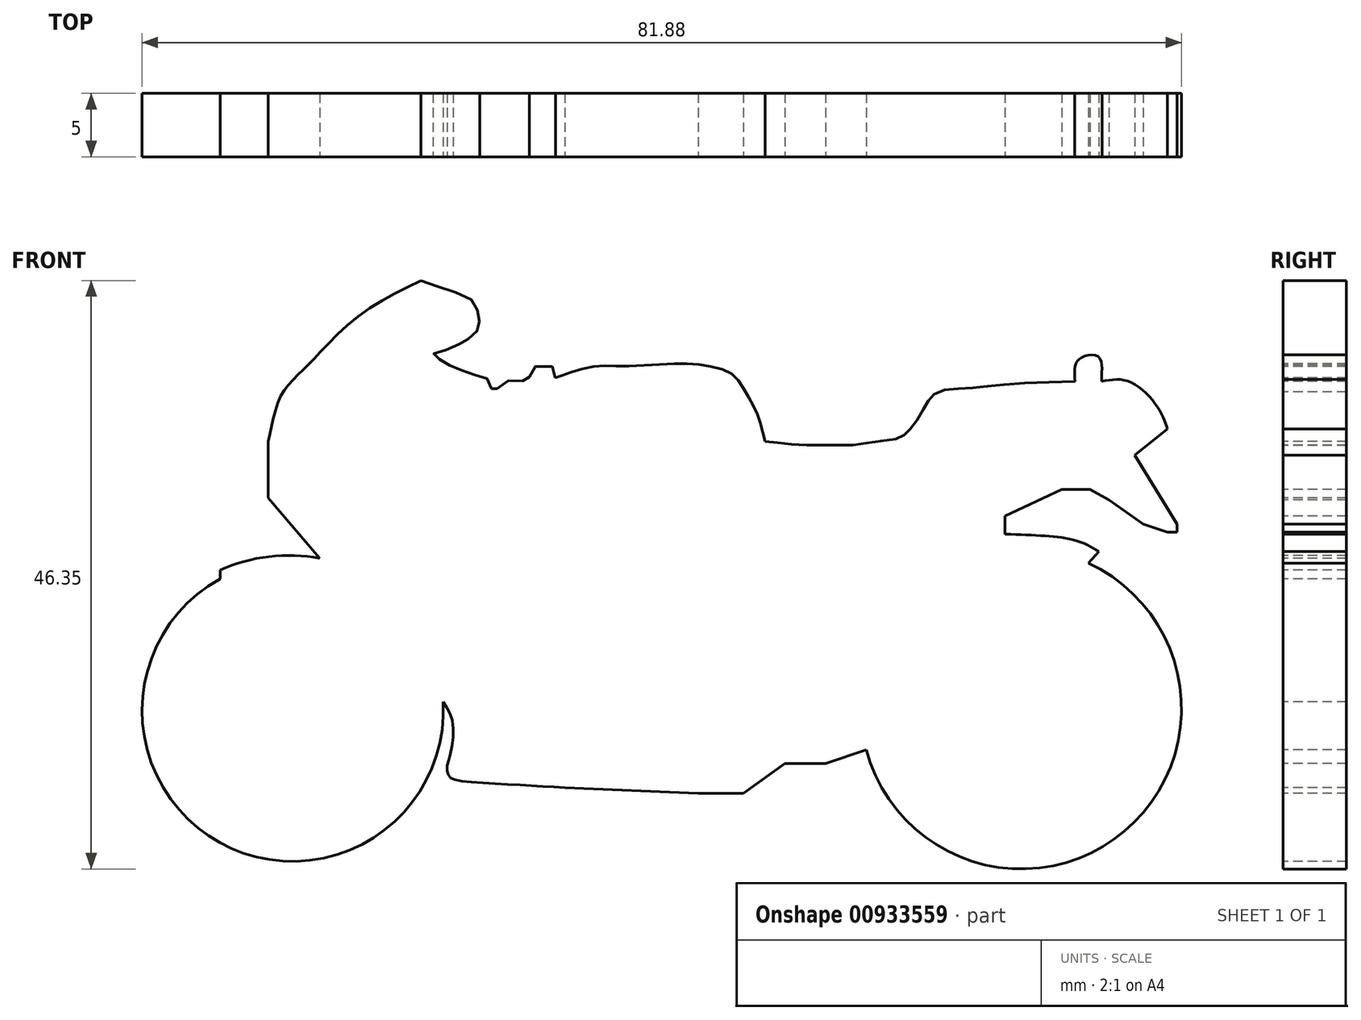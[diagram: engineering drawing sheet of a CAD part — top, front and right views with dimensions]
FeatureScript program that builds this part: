
annotation { "Feature Type Name" : "Feature", "Feature Type Description" : "" }
export const myFeature = defineFeature(function(context is Context, id is Id, definition is map)
    precondition{}
    {
        {
            var Q0;
            Q0=qCreatedBy(makeId("Front.planeOp"),FACE);
            var sketch = newSketch(context, id + "F0", { "sketchPlane" : qUnion([Q0])});
            skArc(sketch, "E0", {"start": v(-70.16, 1.42) * mm, "mid": v(-70.21, -40.14) * mm, "end": v(-35.04, -18) * mm});
            skArc(sketch, "E1", {"start": v(-54.46, 4.66) * mm, "mid": v(-62.45, 4.92) * mm, "end": v(-70.16, 2.8) * mm});
            skLineSegment(sketch, "E2", {"start": v(-70.16, 2.8) * mm, "end": v(-70.16, 1.42) * mm});
            skLineSegment(sketch, "E3", {"start": v(-54.46, 4.66) * mm, "end": v(-62.6, 14.14) * mm});
            skLineSegment(sketch, "E4", {"start": v(-62.6, 23.05) * mm, "end": v(-62.6, 14.14) * mm});
            skFitSpline(sketch, "E5", {"points": [v(-62.6, 23.05) * mm, v(-61.9, 26.19) * mm, v(-60.75, 29.94) * mm, v(-59.4, 31.96) * mm, v(-57.38, 34.08) * mm, v(-54.97, 36.48) * mm, v(-48.72, 42.54) * mm, v(-38.52, 48.41) * mm], "startDerivative": vector(5.38, 25.5) * mm, "endDerivative": vector(48.04, 23.54) * mm});
            skFitSpline(sketch, "E6", {"points": [v(-38.52, 48.41) * mm, v(-34.38, 46.97) * mm, v(-30.34, 45.24) * mm, v(-29.57, 43.4) * mm, v(-29.28, 41.68) * mm, v(-29.76, 40.33) * mm, v(-31.3, 39.08) * mm, v(-32.65, 38.3) * mm, v(-35.34, 37.25) * mm, v(-36.6, 36.77) * mm, v(-35.44, 35.9) * mm, v(-33.8, 34.94) * mm, v(-31.59, 34.08) * mm, v(-29, 33.2) * mm, v(-27.55, 32.44) * mm, v(-27.26, 30.9) * mm, v(-25.82, 32.06) * mm, v(-23.6, 32.73) * mm, v(-21.49, 32.73) * mm, v(-21.3, 34.36) * mm, v(-17.83, 34.85) * mm, v(-17.35, 33.11) * mm], "startDerivative": vector(57.73, -21.29) * mm, "endDerivative": vector(-4, -47.72) * mm});
            skFitSpline(sketch, "E7", {"points": [v(-17.35, 33.11) * mm, v(-15.32, 33.8) * mm, v(-11.03, 34.9) * mm, v(-6.58, 34.9) * mm, v(0.95, 35.3) * mm, v(6.13, 35.06) * mm, v(10.25, 33.8) * mm, v(12.11, 31.66) * mm, v(13.9, 28.67) * mm, v(14.95, 26) * mm, v(15.67, 23.05) * mm], "startDerivative": vector(24.4, 8.5) * mm, "endDerivative": vector(7.65, -34.2) * mm});
            skFitSpline(sketch, "E8", {"points": [v(15.67, 23.05) * mm, v(18.48, 22.76) * mm, v(22.2, 22.47) * mm, v(26.77, 22.47) * mm, v(30.05, 22.55) * mm, v(33.2, 23.05) * mm, v(36.73, 23.56) * mm, v(37.78, 24.21) * mm, v(38.7, 25.18) * mm, v(40.04, 27.08) * mm, v(41.14, 28.99) * mm, v(41.87, 30.04) * mm, v(43.17, 30.96) * mm, v(46.23, 31.37) * mm, v(49.7, 31.64) * mm, v(54.53, 32.11) * mm, v(64.54, 32.5) * mm], "startDerivative": vector(45.35, -4.7) * mm, "endDerivative": vector(95.81, 2.47) * mm});
            skFitSpline(sketch, "E9", {"points": [v(64.54, 32.5) * mm, v(64.54, 34.85) * mm, v(65.6, 36.3) * mm, v(68.26, 36.35) * mm, v(68.75, 33.8) * mm, v(68.75, 32.5) * mm], "startDerivative": vector(-1.02, 11.74) * mm, "endDerivative": vector(0.17, -6.99) * mm});
            skFitSpline(sketch, "E10", {"points": [v(68.75, 32.5) * mm, v(73.05, 32.5) * mm, v(77.57, 28.43) * mm, v(79.11, 25.02) * mm], "startDerivative": vector(13.35, 2.6) * mm, "endDerivative": vector(3.66, -10.87) * mm});
            skLineSegment(sketch, "E11", {"start": v(79.11, 25.02) * mm, "end": v(73.96, 20.89) * mm});
            skLineSegment(sketch, "E12", {"start": v(73.96, 20.89) * mm, "end": v(80.6, 10.07) * mm});
            skLineSegment(sketch, "E13", {"start": v(80.6, 10.07) * mm, "end": v(80.6, 8.77) * mm});
            skLineSegment(sketch, "E14", {"start": v(80.6, 8.77) * mm, "end": v(79.11, 8.77) * mm});
            skLineSegment(sketch, "E15", {"start": v(79.11, 8.77) * mm, "end": v(75.26, 10.07) * mm});
            skLineSegment(sketch, "E16", {"start": v(75.26, 10.07) * mm, "end": v(69.87, 13.88) * mm});
            skLineSegment(sketch, "E17", {"start": v(69.87, 13.88) * mm, "end": v(66.89, 15.51) * mm});
            skLineSegment(sketch, "E18", {"start": v(66.89, 15.51) * mm, "end": v(62.41, 15.51) * mm});
            skLineSegment(sketch, "E19", {"start": v(62.41, 15.51) * mm, "end": v(53.51, 11.3) * mm});
            skLineSegment(sketch, "E20", {"start": v(53.51, 11.3) * mm, "end": v(53.51, 8.48) * mm});
            skFitSpline(sketch, "E21", {"points": [v(53.51, 8.48) * mm, v(59.2, 8.22) * mm, v(62.97, 7.85) * mm, v(66.2, 6.88) * mm, v(68.25, 5.73) * mm], "startDerivative": vector(19.3, -0.82) * mm, "endDerivative": vector(9.61, -5.99) * mm});
            skLineSegment(sketch, "E22", {"start": v(68.25, 5.73) * mm, "end": v(66.61, 3.89) * mm});
            skArc(sketch, "E23", {"start": v(31.64, -25.54) * mm, "mid": v(72.3, -38.37) * mm, "end": v(66.61, 3.89) * mm});
            skLineSegment(sketch, "E24", {"start": v(31.64, -25.54) * mm, "end": v(25.22, -27.66) * mm});
            skLineSegment(sketch, "E25", {"start": v(25.22, -27.66) * mm, "end": v(18.81, -27.66) * mm});
            skLineSegment(sketch, "E26", {"start": v(18.81, -27.66) * mm, "end": v(12.3, -32.35) * mm});
            skLineSegment(sketch, "E27", {"start": v(12.3, -32.35) * mm, "end": v(5.2, -32.35) * mm});
            skLineSegment(sketch, "E28", {"start": v(5.2, -32.35) * mm, "end": v(-15.86, -31.48) * mm});
            skFitSpline(sketch, "E29", {"points": [v(-15.86, -31.48) * mm, v(-24.83, -30.97) * mm, v(-32.93, -30.3) * mm, v(-34.09, -29.67) * mm, v(-34.4, -28.33) * mm, v(-33.8, -25.82) * mm, v(-33.6, -20.92) * mm, v(-35.04, -18) * mm], "startDerivative": vector(-39.5, 2.3) * mm, "endDerivative": vector(-13.64, 19.69) * mm});
            skSolve(sketch);
        }
        {
            var Q0;
            Q0=qCreatedBy(makeId("Front.planeOp"),FACE);
            var sketch = newSketch(context, id + "F1", { "sketchPlane" : qUnion([Q0])});
            skFitSpline(sketch, "E30", {"points": [v(-35.04, -17.89) * mm, v(-36.13, -15.41) * mm, v(-37.85, -13.14) * mm, v(-39.42, -11.13) * mm, v(-41.21, -10.1) * mm, v(-43.1, -8.52) * mm, v(-47.02, -3.87) * mm, v(-51.75, 2.17) * mm, v(-54.44, 4.56) * mm], "startDerivative": vector(-8.4, 23.4) * mm, "endDerivative": vector(-20.39, 15.9) * mm});
            skSolve(sketch);
        }
        {
            var Q0;
            Q0 = qSketchRegion(id + "F0", true);
            extrude(context, id + "F2", {"entities" : qUnion([Q0]), "oppositeDirection" : true, "depth" : 10 * mm, "offsetDistance" : 25 * mm});
        }
        {
            var Q0;
            Q0 = qSketchRegion(id + "F1", true);
            var Q1;
            Q1 = qConstructionFilter(qBodyType(qCreatedBy(id + "F1" ,EDGE), BodyType.WIRE), ConstructionObject.NO);
            extrude(context, id + "F3", {"entities" : qUnion([Q0]), "bodyType" : ToolBodyType.SURFACE, "surfaceEntities" : qUnion([Q1]), "oppositeDirection" : true, "depth" : 10 * mm, "offsetDistance" : 25 * mm});
        }
        {
            var Q0;
            Q0=qCreatedBy(makeId("Front.planeOp"),FACE);
            var sketch = newSketch(context, id + "F4", { "sketchPlane" : qUnion([Q0])});
            skFitSpline(sketch, "E31", {"points": [v(-36.43, 36.87) * mm, v(-40.84, 35.93) * mm, v(-44.62, 34.2) * mm, v(-47.92, 32.62) * mm, v(-50.44, 30.89) * mm, v(-51.39, 29.31) * mm, v(-50.92, 27.58) * mm, v(-49.81, 25.69) * mm, v(-47.3, 22.85) * mm, v(-45.72, 21.75) * mm, v(-43.36, 21.12) * mm, v(-39.9, 20.02) * mm, v(-32.96, 17.81) * mm, v(-28.08, 16.24) * mm, v(-20.2, 13.88) * mm, v(-16.43, 12.15) * mm, v(-12.33, 9.78) * mm, v(-7.92, 7.26) * mm, v(-3.99, 4.74) * mm, v(-1.3, 2.85) * mm, v(4.2, -1.71) * mm, v(8.46, -4.4) * mm, v(8.93, -6.28) * mm, v(9.09, -8.01) * mm, v(8.46, -9.9) * mm, v(7.04, -11.32) * mm, v(5.15, -12.74) * mm, v(2.47, -14.94) * mm, v(0, -16.2) * mm, v(-2.73, -17.78) * mm, v(-4.77, -19.2) * mm, v(-6.66, -22.19) * mm, v(-5.88, -25.18) * mm, v(-3.83, -27.23) * mm, v(-1.3, -28.17) * mm, v(3.57, -28.33) * mm, v(6.88, -28.96) * mm, v(9.72, -30.06) * mm, v(12.55, -32.42) * mm], "startDerivative": vector(-150.53, -23.27) * mm, "endDerivative": vector(101.44, -97.67) * mm});
            skSolve(sketch);
        }
        {
            var Q0;
            Q0 = qSketchRegion(id + "F4", true);
            var Q1;
            Q1 = qConstructionFilter(qBodyType(qCreatedBy(id + "F4" ,EDGE), BodyType.WIRE), ConstructionObject.NO);
            extrude(context, id + "F5", {"entities" : qUnion([Q0]), "bodyType" : ToolBodyType.SURFACE, "surfaceEntities" : qUnion([Q1]), "oppositeDirection" : true, "depth" : 10 * mm, "offsetDistance" : 25 * mm});
        }
        {
            var Q0;
            Q0=qCreatedBy(makeId("Front.planeOp"),FACE);
            var sketch = newSketch(context, id + "F6", { "sketchPlane" : qUnion([Q0])});
            skFitSpline(sketch, "E32", {"points": [v(-26.98, 30.57) * mm, v(-27.92, 26.95) * mm, v(-28.87, 24.43) * mm, v(-28.55, 22.38) * mm, v(-15.64, 19.07) * mm, v(-5.25, 16.71) * mm, v(4.83, 14.5) * mm, v(13.8, 12.46) * mm, v(17.43, 11.99) * mm, v(19, 12.78) * mm, v(18.85, 14.35) * mm, v(16.96, 17.34) * mm, v(15.7, 20.65) * mm, v(15.86, 23.01) * mm], "startDerivative": vector(-12.38, -55) * mm, "endDerivative": vector(7.16, 41.25) * mm});
            skSolve(sketch);
        }
        {
            var Q0;
            Q0 = qSketchRegion(id + "F6", true);
            var Q1;
            Q1 = qConstructionFilter(qBodyType(qCreatedBy(id + "F6" ,EDGE), BodyType.WIRE), ConstructionObject.NO);
            extrude(context, id + "F7", {"entities" : qUnion([Q0]), "bodyType" : ToolBodyType.SURFACE, "surfaceEntities" : qUnion([Q1]), "oppositeDirection" : true, "depth" : 10 * mm, "offsetDistance" : 25 * mm});
        }
        {
            var Q0;
            Q0=qCreatedBy(makeId("Front.planeOp"),FACE);
            var sketch = newSketch(context, id + "F8", { "sketchPlane" : qUnion([Q0])});
            skFitSpline(sketch, "E33", {"points": [v(19.48, 13.1) * mm, v(25.62, 13.56) * mm, v(31.6, 13.88) * mm, v(37.12, 14.5) * mm, v(41.68, 15.92) * mm, v(44.52, 18.44) * mm, v(46.72, 21.28) * mm, v(50.5, 23.33) * mm, v(53.97, 24.9) * mm, v(59.16, 26) * mm, v(62.47, 26.95) * mm, v(65.15, 27.74) * mm, v(65.3, 29.63) * mm, v(64.68, 32.3) * mm], "startDerivative": vector(64.91, 5.57) * mm, "endDerivative": vector(-10.97, 42.45) * mm});
            skSolve(sketch);
        }
        {
            var Q0;
            Q0 = qSketchRegion(id + "F8", true);
            var Q1;
            Q1 = qConstructionFilter(qBodyType(qCreatedBy(id + "F8" ,EDGE), BodyType.WIRE), ConstructionObject.NO);
            extrude(context, id + "F9", {"entities" : qUnion([Q0]), "bodyType" : ToolBodyType.SURFACE, "surfaceEntities" : qUnion([Q1]), "oppositeDirection" : true, "depth" : 10 * mm, "offsetDistance" : 25 * mm});
        }
        {
            var Q0;
            Q0=qCreatedBy(makeId("Front.planeOp"),FACE);
            var sketch = newSketch(context, id + "F10", { "sketchPlane" : qUnion([Q0])});
            skFitSpline(sketch, "E34", {"points": [v(53.65, 11.04) * mm, v(49.24, 8.37) * mm, v(45.94, 6.48) * mm, v(42.63, 4.59) * mm, v(39.8, 3.64) * mm, v(36.01, 4.74) * mm, v(31.6, 6.16) * mm, v(28.3, 7.26) * mm, v(25.15, 7.9) * mm, v(21.21, 9.15) * mm, v(19.8, 10.57) * mm, v(19.64, 13.1) * mm], "startDerivative": vector(-41.78, -25.76) * mm, "endDerivative": vector(1.9, 35.9) * mm});
            skSolve(sketch);
        }
        {
            var Q0;
            Q0 = qConstructionFilter(qBodyType(qCreatedBy(id + "F10" ,EDGE), BodyType.WIRE), ConstructionObject.NO);
            extrude(context, id + "F11", {"bodyType" : ToolBodyType.SURFACE, "surfaceEntities" : qUnion([Q0]), "oppositeDirection" : true, "depth" : 10 * mm, "offsetDistance" : 25 * mm});
        }
        {
            var Q0;
            Q0=makeQuery(id+"F0.imprint","IMPRINT",FACE,{"disambiguationData":[TD([[makeQuery(id+"F0.imprint","IMPRINT",EDGE,{"derivedFrom":sQuery(id+"F0.wireOp",EDGE,"E0")}),1.0]])]});
            var sketch = newSketch(context, id + "F12", { "sketchPlane" : qUnion([Q0])});
            skArc(sketch, "E35", {"start": v(40.75, 3.6) * mm, "mid": v(31.05, -9.38) * mm, "end": v(31.69, -25.56) * mm});
            skSolve(sketch);
        }
        {
            var Q0;
            Q0=makeQuery(id+"F0.imprint","IMPRINT",FACE,{"disambiguationData":[TD([[makeQuery(id+"F0.imprint","IMPRINT",EDGE,{"derivedFrom":sQuery(id+"F0.wireOp",EDGE,"E0")}),1.0]])]});
            var Q1;
            Q1=sQuery(id+"F12.wireOp",EDGE,"E35");
            extrude(context, id + "F13", {"entities" : qUnion([Q0]), "bodyType" : ToolBodyType.SURFACE, "surfaceEntities" : qUnion([Q1]), "oppositeDirection" : true, "depth" : 10 * mm, "offsetDistance" : 25 * mm});
        }
        {
            var Q0;
            Q0=makeQuery(id+"F2.opExtrude","SWEPT_BODY",BODY,{"disambiguationData":[OSD([sQuery(id+"F0.wireOp",EDGE,"E0"),sQuery(id+"F0.wireOp",EDGE,"E1"),sQuery(id+"F0.wireOp",EDGE,"E2"),sQuery(id+"F0.wireOp",EDGE,"E3"),sQuery(id+"F0.wireOp",EDGE,"E4"),sQuery(id+"F0.wireOp",EDGE,"E5"),sQuery(id+"F0.wireOp",EDGE,"E6"),sQuery(id+"F0.wireOp",EDGE,"E7"),sQuery(id+"F0.wireOp",EDGE,"E8"),sQuery(id+"F0.wireOp",EDGE,"E9"),sQuery(id+"F0.wireOp",EDGE,"E10"),sQuery(id+"F0.wireOp",EDGE,"E11"),sQuery(id+"F0.wireOp",EDGE,"E12"),sQuery(id+"F0.wireOp",EDGE,"E13"),sQuery(id+"F0.wireOp",EDGE,"E14"),sQuery(id+"F0.wireOp",EDGE,"E15"),sQuery(id+"F0.wireOp",EDGE,"E16"),sQuery(id+"F0.wireOp",EDGE,"E17"),sQuery(id+"F0.wireOp",EDGE,"E18"),sQuery(id+"F0.wireOp",EDGE,"E19"),sQuery(id+"F0.wireOp",EDGE,"E20"),sQuery(id+"F0.wireOp",EDGE,"E21"),sQuery(id+"F0.wireOp",EDGE,"E22"),sQuery(id+"F0.wireOp",EDGE,"E23"),sQuery(id+"F0.wireOp",EDGE,"E24"),sQuery(id+"F0.wireOp",EDGE,"E25"),sQuery(id+"F0.wireOp",EDGE,"E26"),sQuery(id+"F0.wireOp",EDGE,"E27"),sQuery(id+"F0.wireOp",EDGE,"E28"),sQuery(id+"F0.wireOp",EDGE,"E29")])]});
            var Q1;
            Q1=makeQuery(id+"F3.opExtrude","SWEPT_BODY",BODY,{"disambiguationData":[OSD([sQuery(id+"F1.wireOp",EDGE,"E30")])]});
            var Q2;
            Q2=makeQuery(id+"F5.opExtrude","SWEPT_BODY",BODY,{"disambiguationData":[OSD([sQuery(id+"F4.wireOp",EDGE,"E31")])]});
            var Q3;
            Q3=makeQuery(id+"F7.opExtrude","SWEPT_BODY",BODY,{"disambiguationData":[OSD([sQuery(id+"F6.wireOp",EDGE,"E32")])]});
            var Q4;
            Q4=makeQuery(id+"F11.opExtrude","SWEPT_BODY",BODY,{"disambiguationData":[OSD([sQuery(id+"F10.wireOp",EDGE,"E34")])]});
            var Q5;
            Q5=makeQuery(id+"F9.opExtrude","SWEPT_BODY",BODY,{"disambiguationData":[OSD([sQuery(id+"F8.wireOp",EDGE,"E33")])]});
            var Q6;
            Q6=makeQuery(id+"F13.opExtrude","SWEPT_BODY",BODY,{"disambiguationData":[OSD([sQuery(id+"F12.wireOp",EDGE,"E35")])]});
            var Q7;
            Q7=makeQuery(id+"F2.opExtrude","CAP_VERTEX",VERTEX,{"disambiguationData":[OSD([sQuery(id+"F0.wireOp",EDGE,"E5"),sQuery(id+"F0.wireOp",EDGE,"E6")])],"isStart":true});
            transform(context, id + "F14", {"entities" : qUnion([Q0, Q1, Q2, Q3, Q4, Q5, Q6]), "transformType" : TransformType.SCALE_UNIFORMLY, "scale" : 0.5, "scalePoint" : qUnion([Q7]), "makeCopy" : false});
        }
    });
